annotation { "Feature Type Name" : "Feature", "Feature Type Description" : "" }
export const myFeature = defineFeature(function(context is Context, id is Id, definition is map)
    precondition{}
    {
        {
            var Q0;
            Q0=qCreatedBy(makeId("Front.planeOp"),FACE);
            var sketch = newSketch(context, id + "F0", { "sketchPlane" : qUnion([Q0])});
            skLineSegment(sketch, "E0", {"start": v(-17.4, 13.1) * mm, "end": v(-17.4, -2.2) * mm});
            skLineSegment(sketch, "E1", {"start": v(-17.4, -2.2) * mm, "end": v(-14.62, -17.27) * mm});
            skLineSegment(sketch, "E2", {"start": v(17.4, 13.1) * mm, "end": v(17.4, -2.2) * mm});
            skLineSegment(sketch, "E3", {"start": v(17.4, -2.2) * mm, "end": v(14.61, -17.27) * mm});
            skLineSegment(sketch, "E4", {"start": v(14.61, -17.27) * mm, "end": v(-14.62, -17.27) * mm});
            skLineSegment(sketch, "E5", {"start": v(17.4, 13.1) * mm, "end": v(-17.4, 13.1) * mm});
            skPoint(sketch, "E6.orphan", {"position": v(-17.4, 13.5) * mm});
            skSolve(sketch);
        }
        {
            var Q0;
            Q0=makeQuery(id+"F0.imprint","IMPRINT",FACE,{"disambiguationData":[TD([[makeQuery(id+"F0.imprint","IMPRINT",EDGE,{"derivedFrom":sQuery(id+"F0.wireOp",EDGE,"E0")}),1.0]])]});
            extrude(context, id + "F1", {"entities" : qUnion([Q0]), "depth" : 1 * mm});
        }
        {
            var Q0;
            Q0=makeQuery(id+"F1.opExtrude","CAP_FACE",FACE,{"disambiguationData":[OSD([sQuery(id+"F0.wireOp",EDGE,"E0"),sQuery(id+"F0.wireOp",EDGE,"E1"),sQuery(id+"F0.wireOp",EDGE,"E2"),sQuery(id+"F0.wireOp",EDGE,"E3"),sQuery(id+"F0.wireOp",EDGE,"E4"),sQuery(id+"F0.wireOp",EDGE,"E5")])],"isStart":false});
            var sketch = newSketch(context, id + "F2", { "sketchPlane" : qUnion([Q0])});
            skText(sketch, "E7", { "text": "Isaac Parker\n801-808-1030", "fontName": "DroidSansMono.ttf"});
            const initialGuessF2  = {"E7": [-0.015, 0.00503, 1, 0, 0.00297]};
            skSetInitialGuess(sketch, initialGuessF2);
            skSolve(sketch);
        }
        {
            var Q0;
            Q0 = qSketchRegion(id + "F2", true);
            extrude(context, id + "F3", {"entities" : qUnion([Q0]), "operationType" : NewBodyOperationType.ADD, "depth" : .5 * mm});
        }
    });